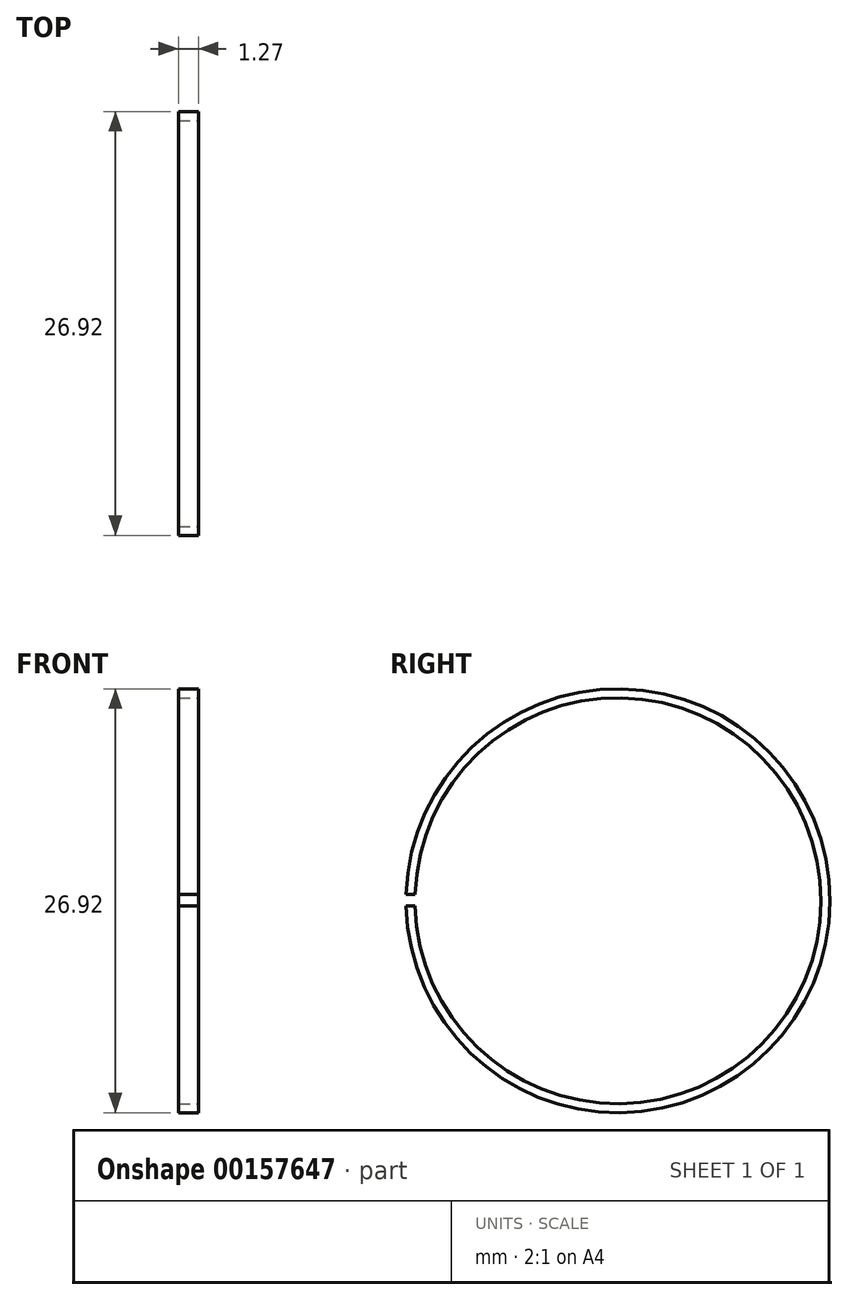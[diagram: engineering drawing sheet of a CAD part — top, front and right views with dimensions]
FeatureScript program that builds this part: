
annotation { "Feature Type Name" : "Feature", "Feature Type Description" : "" }
export const myFeature = defineFeature(function(context is Context, id is Id, definition is map)
    precondition{}
    {
        {
            var Q0;
            Q0=qCreatedBy(makeId("Right.planeOp"),FACE);
            var sketch = newSketch(context, id + "F0", { "sketchPlane" : qUnion([Q0])});
            skArc(sketch, "E0", {"start": v(-13.46, -0.32) * mm, "mid": v(13.46, -0.05) * mm, "end": v(-13.46, 0.41) * mm});
            skArc(sketch, "E1", {"start": v(-12.89, -0.32) * mm, "mid": v(12.9, -0.05) * mm, "end": v(-12.88, 0.41) * mm});
            skLineSegment(sketch, "E2", {"start": v(-13.46, 0.41) * mm, "end": v(-12.88, 0.41) * mm});
            skLineSegment(sketch, "E3", {"start": v(-13.46, -0.32) * mm, "end": v(-12.89, -0.32) * mm});
            skSolve(sketch);
        }
        {
            var Q0;
            Q0=makeQuery(id+"F0.imprint","IMPRINT",FACE,{"disambiguationData":[TD([[makeQuery(id+"F0.imprint","IMPRINT",EDGE,{"derivedFrom":sQuery(id+"F0.wireOp",EDGE,"E0")}),1.0]])]});
            extrude(context, id + "F1", {"entities" : qUnion([Q0]), "oppositeDirection" : true, "depth" : 1.27 * mm});
        }
    });
